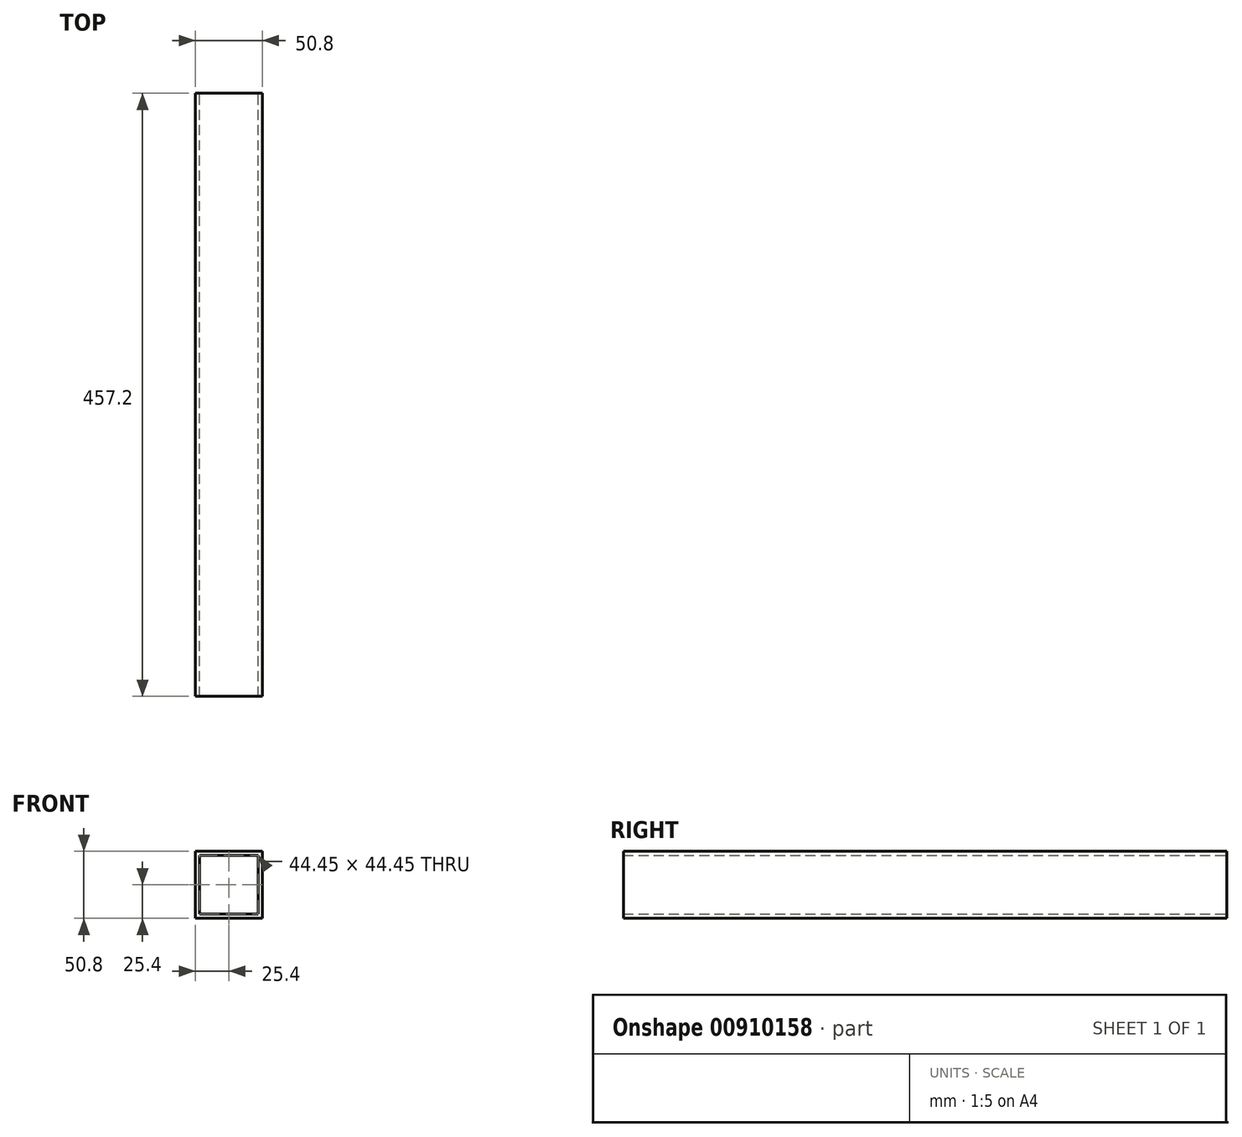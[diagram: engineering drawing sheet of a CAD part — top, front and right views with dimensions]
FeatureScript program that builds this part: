
annotation { "Feature Type Name" : "Feature", "Feature Type Description" : "" }
export const myFeature = defineFeature(function(context is Context, id is Id, definition is map)
    precondition{}
    {
        {
            var Q0;
            Q0=qCreatedBy(makeId("Front.planeOp"),FACE);
            var sketch = newSketch(context, id + "F0", { "sketchPlane" : qUnion([Q0])});
            skLineSegment(sketch, "E0.bottom", {"start": v(-25.4, 25.4) * mm, "end": v(25.4, 25.4) * mm});
            skLineSegment(sketch, "E0.top", {"start": v(-25.4, -25.4) * mm, "end": v(25.4, -25.4) * mm});
            skLineSegment(sketch, "E0.left", {"start": v(-25.4, 25.4) * mm, "end": v(-25.4, -25.4) * mm});
            skLineSegment(sketch, "E0.right", {"start": v(25.4, 25.4) * mm, "end": v(25.4, -25.4) * mm});
            skPoint(sketch, "E0.middle", {"position": v(0, 0) * mm});
            skSolve(sketch);
        }
        {
            var Q0;
            Q0 = qSketchRegion(id + "F0", true);
            extrude(context, id + "F1", {"entities" : qUnion([Q0]), "endBound" : BoundingType.SYMMETRIC, "depth" : 457.2 * mm, "offsetDistance" : 25.4 * mm});
        }
        {
            var Q0;
            Q0=makeQuery(id+"F1.opExtrude","CAP_FACE",FACE,{"disambiguationData":[OSD([sQuery(id+"F0.wireOp",EDGE,"E0.bottom"),sQuery(id+"F0.wireOp",EDGE,"E0.top"),sQuery(id+"F0.wireOp",EDGE,"E0.left"),sQuery(id+"F0.wireOp",EDGE,"E0.right")])],"isStart":false});
            var Q1;
            Q1=makeQuery(id+"F1.opExtrude","CAP_FACE",FACE,{"disambiguationData":[OSD([sQuery(id+"F0.wireOp",EDGE,"E0.bottom"),sQuery(id+"F0.wireOp",EDGE,"E0.top"),sQuery(id+"F0.wireOp",EDGE,"E0.left"),sQuery(id+"F0.wireOp",EDGE,"E0.right")])],"isStart":true});
            shell(context, id + "F2", {"entities" : qUnion([Q0, Q1]), "thickness" : 3.17 * mm});
        }
    });
